# Revit family: ElectricalFixture_WiringAccessories_Hager_Sollyster_RotaryPushButtonDimmers
name_source: partatom
category: Lighting Fixtures
revit_build: Autodesk Revit 2015 (Build: 20160512_1515(x64)
units: mm (PartAtom-declared; Revit-internal decimal feet)

## types (2) — shared parameters
3 Gang = No
4 Gang = No
CE Approval = Yes
Colour = SollystaWhite
Default Elevation = 1219.2 mm  [stored 4 ft]
Design Country = China
Expected Life = 25 years
Extrusion From Wall = 11.9 mm
Finish = Gloss
Frequency = 50/60Hz
Gross Weight kg = 0.165
LED Indicator Switch = No
Manufacturer = Hager
Manufacturer Country = United Kingdom
Manufacturer Website = http://www.hager.co.uk
Material = Urea Formaldehyde Thermoset Plastic
Overall Depth = 26.1 mm
Overall Height = 86 mm  [stored 0.282152 ft]
Overall Length = 86 mm  [stored 0.282152 ft]
Overall Width = 86 mm  [stored 0.282152 ft]
Packaging Recyclable = Yes
Product Family = WhiteMouldedDimmers_RotaryPushButtonDimmers
Product Group = WiringAccessories
Product Literature = http://www.hager.co.uk
Product Range = Sollysta
Product URL = http://www.hager.co.uk
Reference Standard = BS 1363-2
Shape = Rectangular
Shipping Weight kg = 0.188
Supply Phase = 1
Switch = No
Type = ElectricalFixture
Voltage (Volts) = 230V/240V

## per-type parameters (varying)
| type | 1 Gang | 2 Gang | Description | EAN Code | Features | Name | Technical Description |
| WMDR1/400R | Yes | No | 1GangDimmer_60-400W_230V_50/60Hz | 5015654748760 | 1GangDimmer_60-400W_230V_50/60Hz | WhiteMouldedDimmers_WMDR1/400R | 1GangDimmer_60-400W_230V_50/60Hz |
| WMDR2/250R | No | Yes | 2GangDimmer_60-250W/gang_230V_50/60Hz | 5015654748784 | 2GangDimmer_60-250W/gang_230V_50/60Hz | WhiteMouldedDimmers_WMDR2/250R | 2GangDimmer_60-250W/gang_230V_50/60Hz |

note: column(s) folded — value = type name in every type: Product Model Number, Unique Reference

note: [stored X ft] marks values corroborated as IEEE doubles in the binary element streams (Revit-internal decimal feet)

## geometry (parser evidence)
native form markers: Blend x4, Sweep x6
no freeform markers — native parametric forms only
